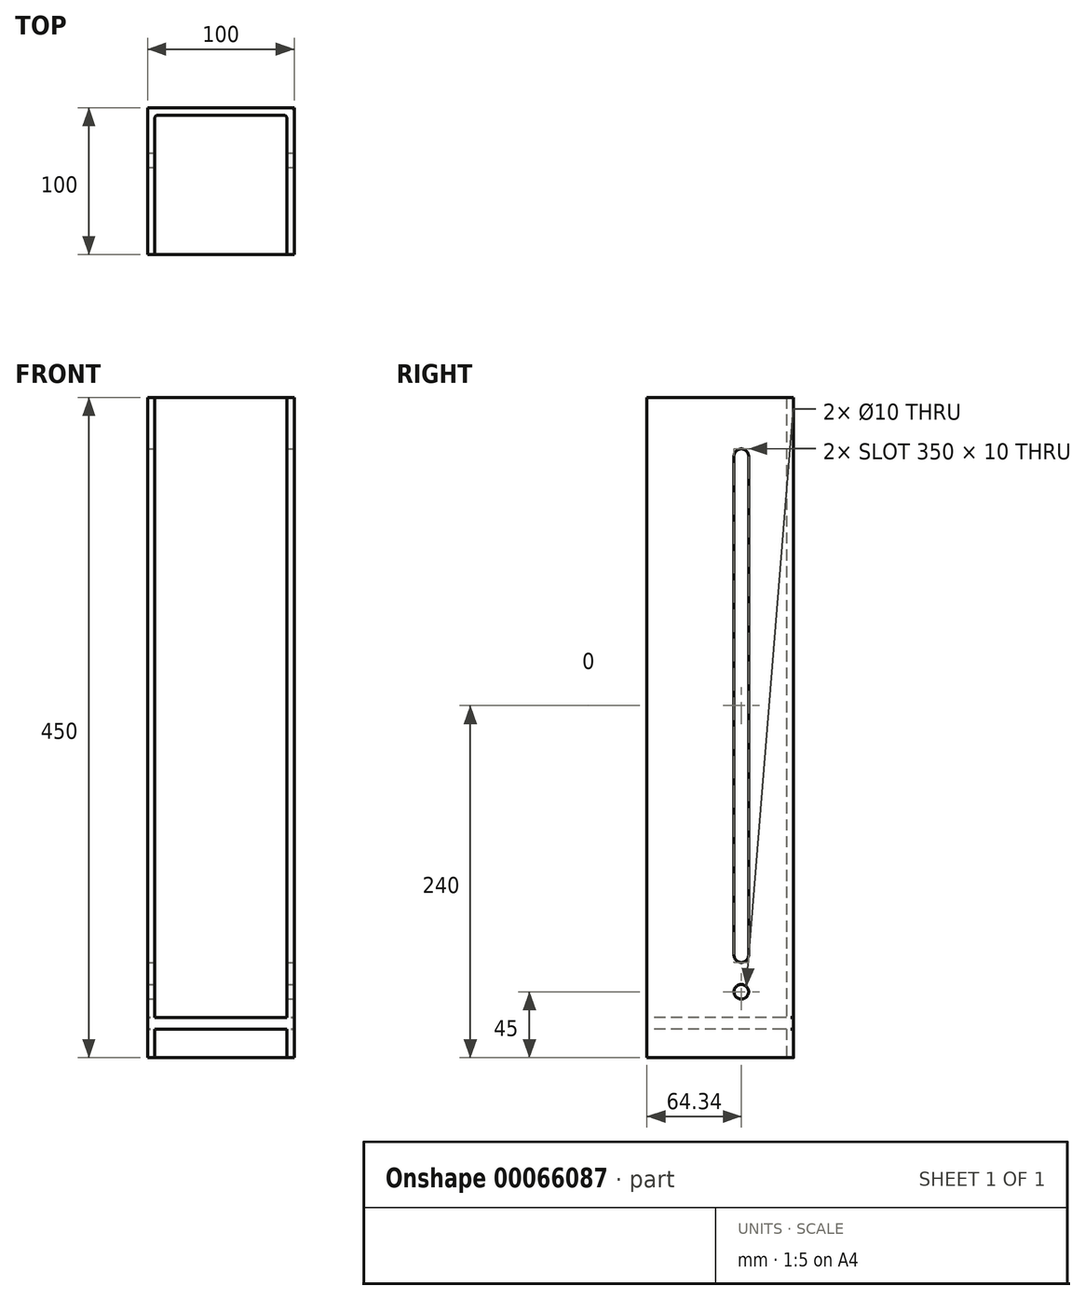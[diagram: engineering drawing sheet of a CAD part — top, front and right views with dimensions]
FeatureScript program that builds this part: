
annotation { "Feature Type Name" : "Feature", "Feature Type Description" : "" }
export const myFeature = defineFeature(function(context is Context, id is Id, definition is map)
    precondition{}
    {
        {
            var Q0;
            Q0=qCreatedBy(makeId("Top.planeOp"),FACE);
            var sketch = newSketch(context, id + "F0", { "sketchPlane" : qUnion([Q0])});
            skLineSegment(sketch, "E0.bottom", {"start": v(-50, -69.34) * mm, "end": v(-45, -69.34) * mm});
            skLineSegment(sketch, "E0.top", {"start": v(-48, 30.66) * mm, "end": v(48, 30.66) * mm});
            skLineSegment(sketch, "E0.left", {"start": v(-50, -69.34) * mm, "end": v(-50, 28.66) * mm});
            skLineSegment(sketch, "E0.right", {"start": v(50, -69.34) * mm, "end": v(50, 28.66) * mm});
            skLineSegment(sketch, "E1.0", {"start": v(45, -69.34) * mm, "end": v(45, 23.66) * mm});
            skLineSegment(sketch, "E1.1", {"start": v(-43, 25.66) * mm, "end": v(43, 25.66) * mm});
            skLineSegment(sketch, "E1.2", {"start": v(-45, -69.34) * mm, "end": v(-45, 23.66) * mm});
            skLineSegment(sketch, "E2.trimOffspring", {"start": v(45, -69.34) * mm, "end": v(50, -69.34) * mm});
            skPoint(sketch, "E3.visualSharp", {"position": v(-45, 25.66) * mm});
            skArc(sketch, "E3.filletArc", {"start": v(-43, 25.66) * mm, "mid": v(-44.41, 25.07) * mm, "end": v(-45, 23.66) * mm});
            skPoint(sketch, "E4.visualSharp", {"position": v(45, 25.66) * mm});
            skArc(sketch, "E4.filletArc", {"start": v(45, 23.66) * mm, "mid": v(44.41, 25.07) * mm, "end": v(43, 25.66) * mm});
            skPoint(sketch, "E5.visualSharp", {"position": v(50, 30.66) * mm});
            skArc(sketch, "E5.filletArc", {"start": v(50, 28.66) * mm, "mid": v(49.41, 30.07) * mm, "end": v(48, 30.66) * mm});
            skPoint(sketch, "E6.visualSharp", {"position": v(-50, 30.66) * mm});
            skArc(sketch, "E6.filletArc", {"start": v(-48, 30.66) * mm, "mid": v(-49.41, 30.07) * mm, "end": v(-50, 28.66) * mm});
            skSolve(sketch);
        }
        {
            var Q0;
            Q0=makeQuery(id+"F0.imprint","IMPRINT",FACE,{"disambiguationData":[TD([[makeQuery(id+"F0.imprint","IMPRINT",EDGE,{"derivedFrom":sQuery(id+"F0.wireOp",EDGE,"E0.bottom")}),1.0]])]});
            extrude(context, id + "F1", {"entities" : qUnion([Q0]), "endBound" : BoundingType.SYMMETRIC, "depth" : 450 * mm});
        }
        {
            var Q0;
            Q0=qCreatedBy(makeId("Right.planeOp"),FACE);
            var sketch = newSketch(context, id + "F2", { "sketchPlane" : qUnion([Q0])});
            skLineSegment(sketch, "E7.bottom", {"start": v(-5, 190) * mm, "end": v(-5, 190) * mm});
            skLineSegment(sketch, "E7.top", {"start": v(-5, -160) * mm, "end": v(-5, -160) * mm});
            skLineSegment(sketch, "E7.left", {"start": v(0, 185) * mm, "end": v(0, -155) * mm});
            skLineSegment(sketch, "E7.right", {"start": v(-10, 185) * mm, "end": v(-10, -155) * mm});
            skPoint(sketch, "E8.visualSharp", {"position": v(0, 190) * mm});
            skArc(sketch, "E8.filletArc", {"start": v(0, 185) * mm, "mid": v(-1.46, 188.54) * mm, "end": v(-5, 190) * mm});
            skPoint(sketch, "E9.visualSharp", {"position": v(-10, 190) * mm});
            skArc(sketch, "E9.filletArc", {"start": v(-5, 190) * mm, "mid": v(-8.54, 188.54) * mm, "end": v(-10, 185) * mm});
            skPoint(sketch, "E10.visualSharp", {"position": v(0, -160) * mm});
            skArc(sketch, "E10.filletArc", {"start": v(-5, -160) * mm, "mid": v(-1.46, -158.54) * mm, "end": v(0, -155) * mm});
            skPoint(sketch, "E11.visualSharp", {"position": v(-10, -160) * mm});
            skArc(sketch, "E11.filletArc", {"start": v(-10, -155) * mm, "mid": v(-8.54, -158.54) * mm, "end": v(-5, -160) * mm});
            skLineSegment(sketch, "E12", {"start": v(-5, -160) * mm, "end": v(-5, -175) * mm});
            skCircle(sketch, "E13", {"center": v(-5, -180) * mm, "radius": 5 * mm});
            skLineSegment(sketch, "E14.bottom", {"start": v(30.66, -197.43) * mm, "end": v(-69.34, -197.43) * mm});
            skLineSegment(sketch, "E14.top", {"start": v(30.66, -205.43) * mm, "end": v(-69.34, -205.43) * mm});
            skLineSegment(sketch, "E14.left", {"start": v(30.66, -197.43) * mm, "end": v(30.66, -205.43) * mm});
            skLineSegment(sketch, "E14.right", {"start": v(-69.34, -197.43) * mm, "end": v(-69.34, -205.43) * mm});
            skSolve(sketch);
        }
        {
            var Q0;
            Q0=makeQuery(id+"F2.imprint","IMPRINT",FACE,{"disambiguationData":[TD([[makeQuery(id+"F2.imprint","IMPRINT",EDGE,{"derivedFrom":sQuery(id+"F2.wireOp",EDGE,"E7.left")}),-1.0]])]});
            var Q1;
            Q1=makeQuery(id+"F2.imprint","IMPRINT",FACE,{"disambiguationData":[TD([[makeQuery(id+"F2.imprint","IMPRINT",EDGE,{"derivedFrom":sQuery(id+"F2.wireOp",EDGE,"E13")}),1.0]])]});
            extrude(context, id + "F3", {"entities" : qUnion([Q0, Q1]), "operationType" : NewBodyOperationType.REMOVE, "endBound" : BoundingType.SYMMETRIC, "oppositeDirection" : true, "depth" : 120 * mm});
        }
        {
            var Q0;
            Q0=makeQuery(id+"F2.imprint","IMPRINT",FACE,{"disambiguationData":[TD([[makeQuery(id+"F2.imprint","IMPRINT",EDGE,{"derivedFrom":sQuery(id+"F2.wireOp",EDGE,"E14.bottom")}),1.0]])]});
            extrude(context, id + "F4", {"entities" : qUnion([Q0]), "operationType" : NewBodyOperationType.ADD, "endBound" : BoundingType.SYMMETRIC, "depth" : 100 * mm});
        }
    });
